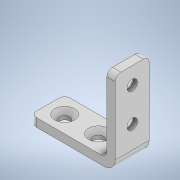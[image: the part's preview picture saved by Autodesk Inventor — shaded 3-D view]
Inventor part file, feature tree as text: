
AUTODESK INVENTOR PART (.ipt)
format: ipt  version: 2021 (Build 250183000, 183)  size: 152,576 bytes
history: native  units: mm
features: sketch x4, extrude x2, hole x2, fillet x2
ambient origin geometry x8: Origin, YZ Plane, XZ Plane, XY Plane, X Axis, Y Axis, Z Axis, Center Point
bodies: Solid1 (feature_tree)
feature tree (10):
  extrude  "Extrusion1"  Depth=12.0mm
  extrude  "Extrusion2"  Depth=3.0mm
  hole  "Hole1"  [1 undecoded]
  hole  "Hole2"  [1 undecoded]
  fillet  "Fillet1"  Radius=18.0mm
  fillet  "Fillet2"  Radius=2.0mm
  sketch  "Sketch1"  dims[d0=30.0mm d1=12.0mm]
  sketch  "Sketch2"  dims[d2=3.0mm d3=0.0mm d4=3.0mm]
  sketch  "Sketch4"  dims[d5=27.0mm d6=0.0mm d7=12.0mm]
  sketch  "Sketch5"  dims[d9=18.0mm d10=3.7mm d11=6.0mm d12=7.0mm d13=2.0mm d14=90.0deg d15=8.0mm d16=20.594885mm d17=12.0mm d18=18.0mm d19=3.7mm d20=6.0mm d21=7.0mm d22=2.0mm d23=90.0deg d24=8.0mm d25=20.594885mm d26=2.0mm d27=4.0mm]
note: 2 required parameter values undecoded (feature->parameter linkage not recoverable at this tier; creation-order binding heuristic only, values carry confidence <= 0.55)
